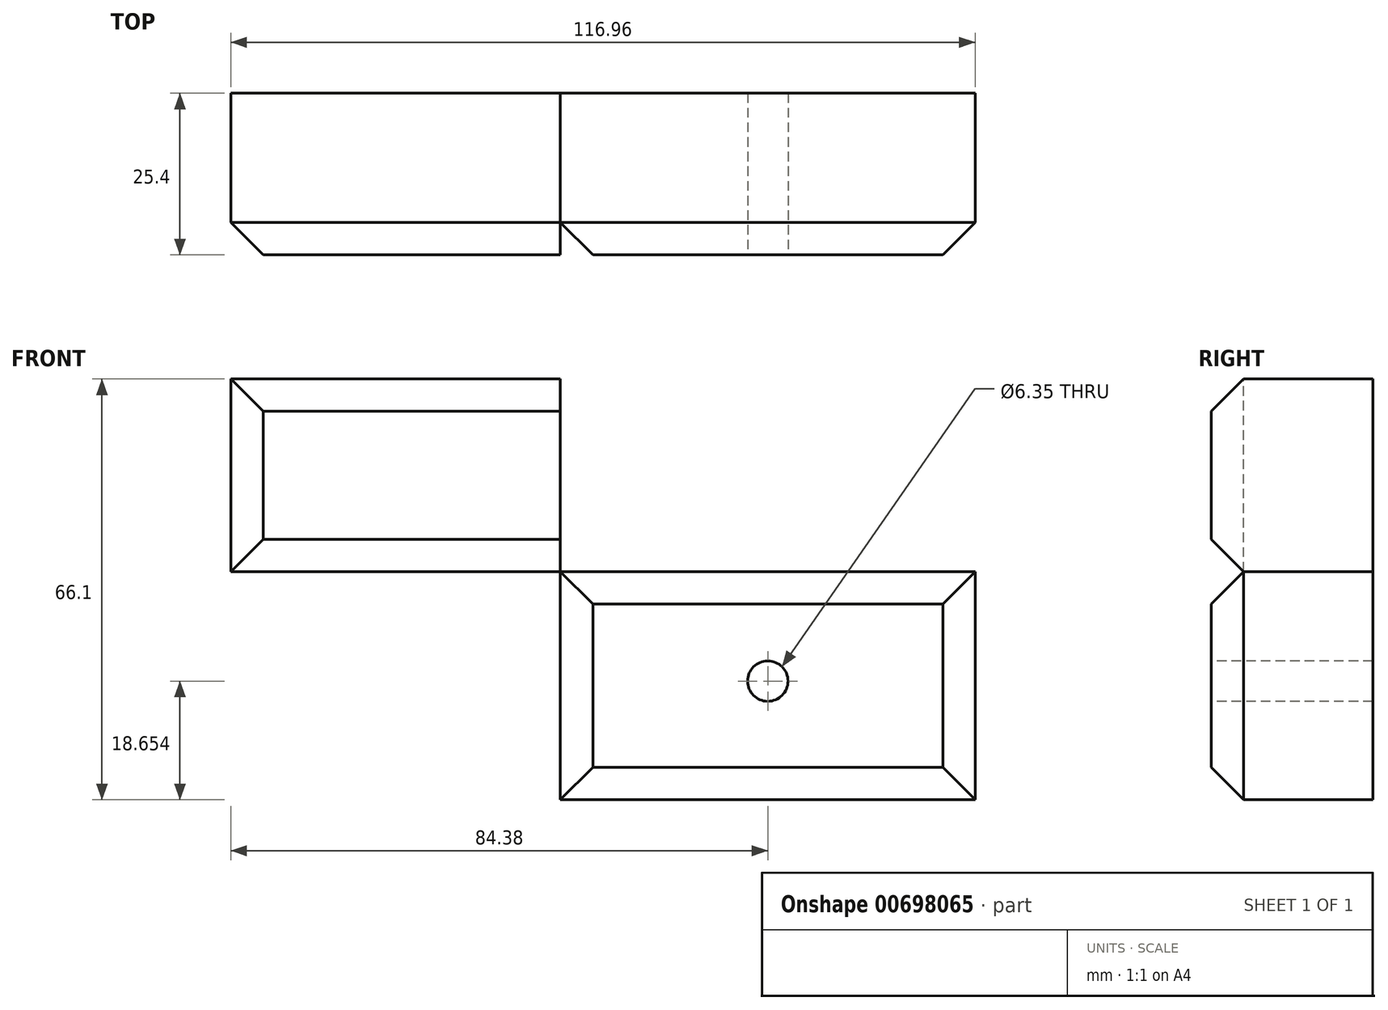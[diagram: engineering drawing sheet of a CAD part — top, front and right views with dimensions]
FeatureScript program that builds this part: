
annotation { "Feature Type Name" : "Feature", "Feature Type Description" : "" }
export const myFeature = defineFeature(function(context is Context, id is Id, definition is map)
    precondition{}
    {
        {
            var Q0;
            Q0=qCreatedBy(makeId("Front.planeOp"),FACE);
            var sketch = newSketch(context, id + "F0", { "sketchPlane" : qUnion([Q0])});
            skLineSegment(sketch, "E0.bottom", {"start": v(0, 47.68) * mm, "end": v(0, 47.68) * mm});
            skLineSegment(sketch, "E0.top", {"start": v(0, 0) * mm, "end": v(0, 0) * mm});
            skLineSegment(sketch, "E0.left", {"start": v(0, 47.68) * mm, "end": v(0, 0) * mm});
            skLineSegment(sketch, "E0.right", {"start": v(0, 47.68) * mm, "end": v(0, 0) * mm});
            skLineSegment(sketch, "E1.bottom", {"start": v(45.1, 47.68) * mm, "end": v(56.17, 47.68) * mm});
            skLineSegment(sketch, "E1.top", {"start": v(45.1, 47.68) * mm, "end": v(56.17, 47.68) * mm});
            skLineSegment(sketch, "E1.left", {"start": v(45.1, 47.68) * mm, "end": v(45.1, 47.68) * mm});
            skLineSegment(sketch, "E1.right", {"start": v(56.17, 47.68) * mm, "end": v(56.17, 47.68) * mm});
            skLineSegment(sketch, "E2.bottom", {"start": v(65.16, -35.87) * mm, "end": v(0, -35.87) * mm});
            skLineSegment(sketch, "E2.top", {"start": v(65.16, 0) * mm, "end": v(0, 0) * mm});
            skLineSegment(sketch, "E2.left", {"start": v(65.16, -35.87) * mm, "end": v(65.16, 0) * mm});
            skLineSegment(sketch, "E2.right", {"start": v(0, -35.87) * mm, "end": v(0, 0) * mm});
            skLineSegment(sketch, "E3.bottom", {"start": v(0, 0) * mm, "end": v(-51.8, 0) * mm});
            skLineSegment(sketch, "E3.top", {"start": v(0, 30.23) * mm, "end": v(-51.8, 30.23) * mm});
            skLineSegment(sketch, "E3.left", {"start": v(0, 0) * mm, "end": v(0, 30.23) * mm});
            skLineSegment(sketch, "E3.right", {"start": v(-51.8, 0) * mm, "end": v(-51.8, 30.23) * mm});
            skSolve(sketch);
        }
        {
            var Q0;
            Q0 = qSketchRegion(id + "F0", true);
            extrude(context, id + "F1", {"entities" : qUnion([Q0]), "depth" : 25.4 * mm, "offsetDistance" : 25.4 * mm});
        }
        {
            var Q0;
            Q0=makeQuery(id+"F1.opExtrude","CAP_FACE",FACE,{"disambiguationData":[OSD([sQuery(id+"F0.wireOp",EDGE,"E2.bottom"),sQuery(id+"F0.wireOp",EDGE,"E2.top"),sQuery(id+"F0.wireOp",EDGE,"E2.left"),sQuery(id+"F0.wireOp",EDGE,"E2.right")])],"isStart":false});
            chamfer(context, id + "F2", {"entities" : qUnion([Q0]), "width" : 5.08 * mm, "tangentPropagation" : true});
        }
        {
            var Q0;
            Q0=makeQuery(id+"F1.opExtrude","CAP_EDGE",EDGE,{"disambiguationData":[OSD([sQuery(id+"F0.wireOp",EDGE,"E3.top")])],"isStart":false});
            var Q1;
            Q1=makeQuery(id+"F1.opExtrude","CAP_EDGE",EDGE,{"disambiguationData":[OSD([sQuery(id+"F0.wireOp",EDGE,"E3.bottom")])],"isStart":false});
            var Q2;
            Q2=makeQuery(id+"F1.opExtrude","CAP_EDGE",EDGE,{"disambiguationData":[OSD([sQuery(id+"F0.wireOp",EDGE,"E3.left")])],"isStart":false});
            var Q3;
            Q3=makeQuery(id+"F1.opExtrude","CAP_EDGE",EDGE,{"disambiguationData":[OSD([sQuery(id+"F0.wireOp",EDGE,"E3.right")])],"isStart":false});
            chamfer(context, id + "F3", {"entities" : qUnion([Q0, Q1, Q2, Q3]), "width" : 5.08 * mm, "tangentPropagation" : true});
        }
        {
            var Q0;
            Q0=makeQuery(id+"F1.opExtrude","CAP_FACE",FACE,{"disambiguationData":[OSD([sQuery(id+"F0.wireOp",EDGE,"E2.bottom"),sQuery(id+"F0.wireOp",EDGE,"E2.top"),sQuery(id+"F0.wireOp",EDGE,"E2.left"),sQuery(id+"F0.wireOp",EDGE,"E2.right")])],"isStart":false});
            var sketch = newSketch(context, id + "F4", { "sketchPlane" : qUnion([Q0])});
            skPoint(sketch, "E4", {"position": v(32.58, -17.22) * mm});
            skPoint(sketch, "E4.positionSnap0", {"position": v(32.58, -30.79) * mm});
            skSolve(sketch);
        }
        {
            var Q0;
            Q0=sQuery(id+"F4.wireOp",VERTEX,"E4");
            var Q1;
            Q1=makeQuery(id+"F1.opExtrude","SWEPT_BODY",BODY,{"disambiguationData":[OSD([sQuery(id+"F0.wireOp",EDGE,"E2.bottom"),sQuery(id+"F0.wireOp",EDGE,"E2.top"),sQuery(id+"F0.wireOp",EDGE,"E2.left"),sQuery(id+"F0.wireOp",EDGE,"E2.right")])]});
            hole(context, id + "F5", {"style" : HoleStyle.SIMPLE, "endStyle" : HoleEndStyle.THROUGH, "holeDiameter" : 6.35 * mm, "majorDiameter" : 6.35 * mm, "isTappedThrough" : true, "tappedDepth" : 12.7 * mm, "tapClearance" : 3, "locations" : qUnion([Q0]), "scope" : qUnion([Q1])});
        }
    });
